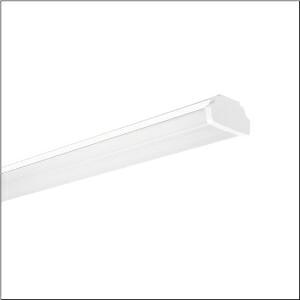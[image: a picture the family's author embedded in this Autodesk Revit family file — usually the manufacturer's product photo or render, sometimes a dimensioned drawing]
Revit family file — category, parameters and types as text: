
# Revit family: modario_r__31_mo_53bm812m1v4085_4dae
name_source: partatom
category: Lighting Fixtures
units: mm (PartAtom-declared; Revit-internal decimal feet)

## family parameters
Cut with Voids When Loaded = No
Host = Face
Light Source = No
Part Type = Normal
Room Calculation Point = No
Round Connector Dimension = Use Diameter
Shared = No

## types (1)
- --- (1 x LED, 8950 lm, 59.6 W, 4000K)
    Apparent Load = 60 VA
    CIE Flux Codes = 47 80 95 92 100
    Color Rendering = 80
    Color Temperature = 4000K
    Default Elevation = 1800 mm
    Description = Modario® 31 MO, luminaire insert, of sheet steel, coil coated, white, length: 1.495mm, width: 81mm, height: 82mm, 5x system unit, system units: 299mm, LED rated luminous flux: 8.950lm, light colour: 840, control gear: ON/OFF Multilumen, control gear: ECG Multilumen, with plug, 3-pole, with phase selection, mains connection: 220..240V, AC, 50/60Hz, rated input power: 60W, through-wiring accessed according to module size, primary optical cover: cover, of PMMA, light emission: direct distribution, primary light characteristic: symmetric, protection rating (complete): IP20, protection rating (LED compartment): IP50, insulation class (complete): insulation class I (protective earthing), certification: CE, ENEC, VDE, UKCA, impact resistance: IK03, permissible ambient temperature for indoor applications: -35..+30°C, corresponds to IFS (International Featured Standards) requirements for safety and quality in the food industry, reducing of maximum allowable ambient temperature of 5°C with ceiling mounting, packaging unit: 1 piece
    Height = 92 mm
    Lamp = 1 x LED
    Lamp Light Flux = 8950 lm
    Lamp Power = 59.6 W
    Lamp count = 1
    Length = 1495 mm
    Luminous efficacy = 150 lm/W
    Manufacturer = Siteco
    ModVariant = No
    Model = 53BM812M1V4085
    Mounting Place = Ceiling
    Mounting Type = Pendant
    Number of Poles = 1
    OnlyDefault = Yes
    Power Factor = 1
    Product Name = Modario® 31 MO
    Product group = luminaire insert
    ProductGroupID = 901
    Protection Class = Protection class I
    Protection Degree = IP 20
    RLX_Detail_Level = 1
    RLX_Emergency_Light_Flux = 0 lm
    RLX_Emergency_Type = 0
    RLX_Emergency_Type_DB = No
    RlxData = <blob elided: 40069 chars, md5=dbe22451>
    Socket = socket
    Standby Power = 0 W
    System Light Flux = 8950 lm
    System Power = 60 W
    Type Comments = factory setting: luminous flux: 100 % | (A | C | E) | 129 mA
    Type Image = l_1300283.jpg
    URL = http://relux.com
    VarID = @adj_140361
    Voltage = 0 V
    Weight = 0.00 kg
    Width = 81 mm

## geometry (parser evidence)
native form markers: Blend x4, Sweep x12
no freeform markers — native parametric forms only
